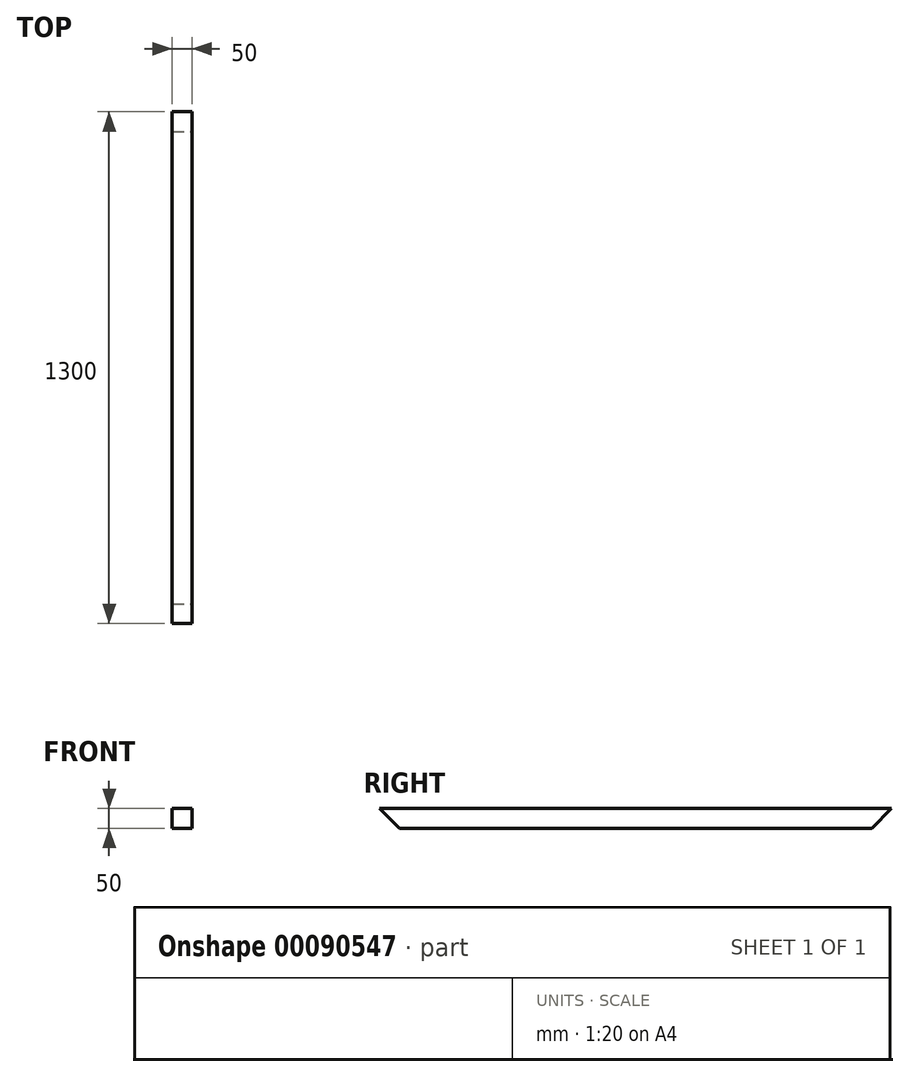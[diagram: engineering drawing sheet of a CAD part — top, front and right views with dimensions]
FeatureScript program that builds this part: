
annotation { "Feature Type Name" : "Feature", "Feature Type Description" : "" }
export const myFeature = defineFeature(function(context is Context, id is Id, definition is map)
    precondition{}
    {
        {
            var Q0;
            Q0=qCreatedBy(makeId("Front.planeOp"),FACE);
            var sketch = newSketch(context, id + "F0", { "sketchPlane" : qUnion([Q0])});
            skLineSegment(sketch, "E0.bottom", {"start": v(25, -25) * mm, "end": v(-25, -25) * mm});
            skLineSegment(sketch, "E0.top", {"start": v(25, 25) * mm, "end": v(-25, 25) * mm});
            skLineSegment(sketch, "E0.left", {"start": v(25, -25) * mm, "end": v(25, 25) * mm});
            skLineSegment(sketch, "E0.right", {"start": v(-25, -25) * mm, "end": v(-25, 25) * mm});
            skPoint(sketch, "E0.middle", {"position": v(0, 0) * mm});
            skSolve(sketch);
        }
        {
            var Q0;
            Q0 = qSketchRegion(id + "F0", true);
            extrude(context, id + "F1", {"entities" : qUnion([Q0]), "depth" : 1300 * mm});
        }
        {
            var Q0;
            Q0=qCreatedBy(makeId("Right.planeOp"),FACE);
            var sketch = newSketch(context, id + "F2", { "sketchPlane" : qUnion([Q0])});
            skLineSegment(sketch, "E1", {"start": v(-1250, -25) * mm, "end": v(-1300, 25) * mm});
            skLineSegment(sketch, "E2", {"start": v(-50, -25) * mm, "end": v(0, 25) * mm});
            skLineSegment(sketch, "E3", {"start": v(-1300, -25) * mm, "end": v(-1250, -25) * mm});
            skLineSegment(sketch, "E4", {"start": v(-1300, 25) * mm, "end": v(-1300, -25) * mm});
            skLineSegment(sketch, "E5", {"start": v(0, 25) * mm, "end": v(0, -25) * mm});
            skLineSegment(sketch, "E6", {"start": v(-50, -25) * mm, "end": v(0, -25) * mm});
            skSolve(sketch);
        }
        {
            var Q0;
            Q0 = qSketchRegion(id + "F2", true);
            extrude(context, id + "F3", {"entities" : qUnion([Q0]), "operationType" : NewBodyOperationType.REMOVE, "endBound" : BoundingType.THROUGH_ALL, "oppositeDirection" : true, "depth" : 25 * mm, "hasSecondDirection" : true, "secondDirectionBound" : SecondDirectionBoundingType.THROUGH_ALL, "secondDirectionOppositeDirection" : false, "secondDirectionDepth" : 25 * mm});
        }
    });
